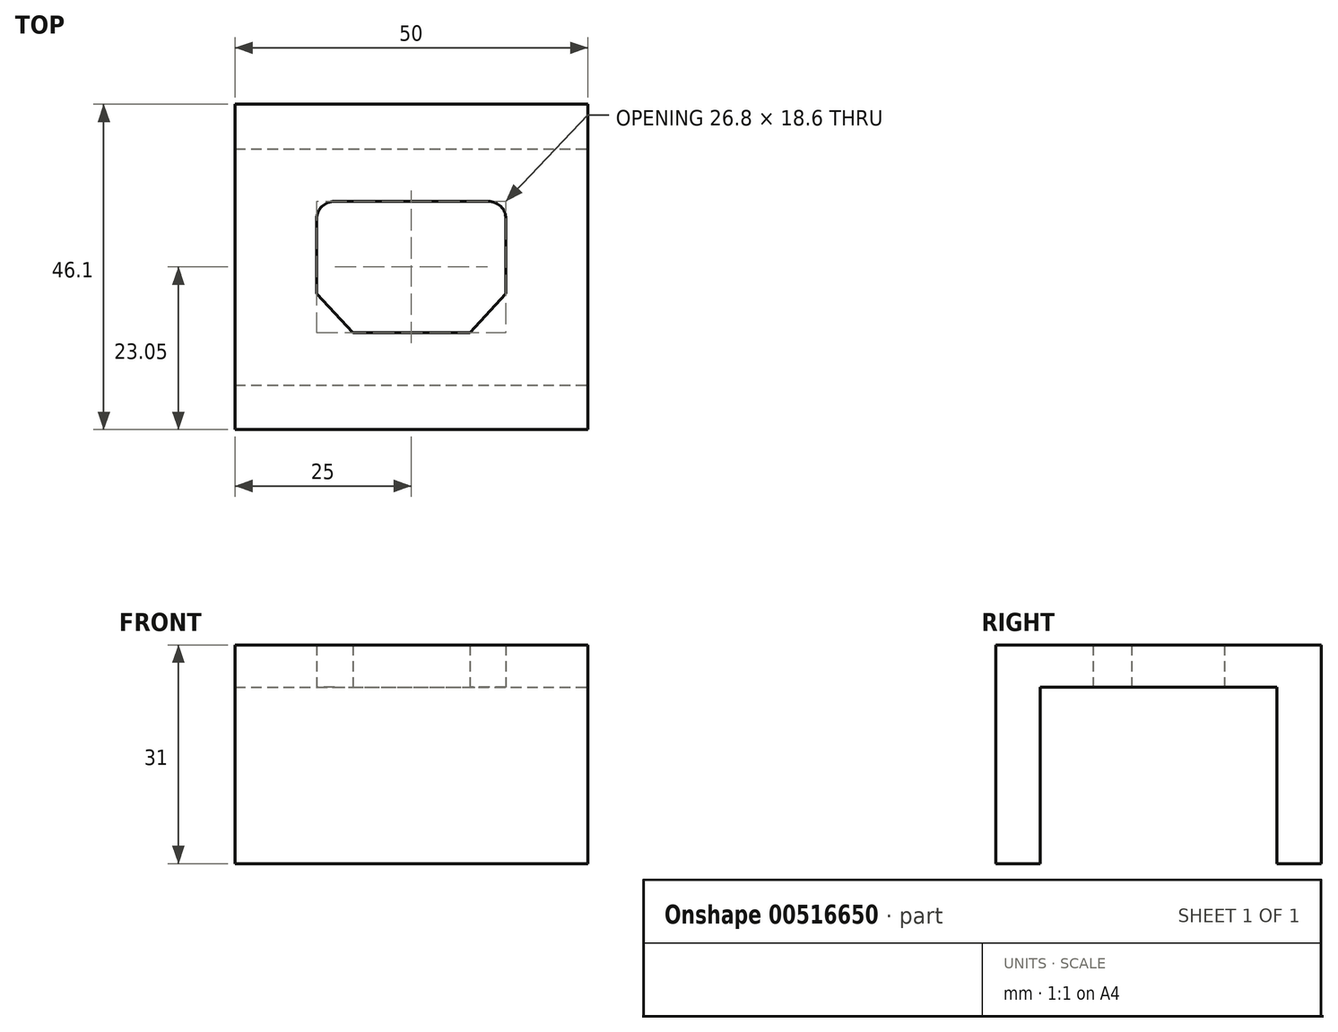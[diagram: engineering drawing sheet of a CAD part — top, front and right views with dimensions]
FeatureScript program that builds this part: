
annotation { "Feature Type Name" : "Feature", "Feature Type Description" : "" }
export const myFeature = defineFeature(function(context is Context, id is Id, definition is map)
    precondition{}
    {
        {
            var Q0;
            Q0=qCreatedBy(makeId("Top.planeOp"),FACE);
            var sketch = newSketch(context, id + "F0", { "sketchPlane" : qUnion([Q0])});
            skLineSegment(sketch, "E0.bottom", {"start": v(-25, 23.05) * mm, "end": v(25, 23.05) * mm});
            skLineSegment(sketch, "E0.top", {"start": v(-25, -23.05) * mm, "end": v(25, -23.05) * mm});
            skLineSegment(sketch, "E0.left", {"start": v(-25, 23.05) * mm, "end": v(-25, -23.05) * mm});
            skLineSegment(sketch, "E0.right", {"start": v(25, 23.05) * mm, "end": v(25, -23.05) * mm});
            skLineSegment(sketch, "E1.bottom", {"start": v(-10.9, 9.3) * mm, "end": v(10.9, 9.3) * mm});
            skLineSegment(sketch, "E1.top", {"start": v(-8.3, -9.3) * mm, "end": v(8.3, -9.3) * mm});
            skLineSegment(sketch, "E1.left", {"start": v(-13.4, 6.8) * mm, "end": v(-13.4, -3.8) * mm});
            skLineSegment(sketch, "E1.right", {"start": v(13.4, 6.8) * mm, "end": v(13.4, -3.8) * mm});
            skLineSegment(sketch, "E2", {"start": v(13.4, -3.8) * mm, "end": v(8.3, -9.3) * mm});
            skLineSegment(sketch, "E3.MirrorCS", {"start": v(-13.4, -3.8) * mm, "end": v(-8.3, -9.3) * mm});
            skPoint(sketch, "E4.orphan", {"position": v(13.4, -9.3) * mm});
            skPoint(sketch, "E5.visualSharp", {"position": v(-13.4, 9.3) * mm});
            skArc(sketch, "E5.filletArc", {"start": v(-10.9, 9.3) * mm, "mid": v(-12.67, 8.57) * mm, "end": v(-13.4, 6.8) * mm});
            skPoint(sketch, "E6.visualSharp", {"position": v(13.4, 9.3) * mm});
            skArc(sketch, "E6.filletArc", {"start": v(13.4, 6.8) * mm, "mid": v(12.67, 8.57) * mm, "end": v(10.9, 9.3) * mm});
            skCircle(sketch, "E7", {"center": v(-19.95, 0) * mm, "radius": 1.75 * mm});
            skCircle(sketch, "E8", {"center": v(19.95, 0) * mm, "radius": 1.75 * mm});
            skSolve(sketch);
        }
        {
            var Q0;
            Q0=makeQuery(id+"F0.imprint","IMPRINT",FACE,{"disambiguationData":[TD([[makeQuery(id+"F0.imprint","IMPRINT",EDGE,{"derivedFrom":sQuery(id+"F0.wireOp",EDGE,"E0.bottom")}),-1.0]])]});
            var Q1;
            Q1=makeQuery(id+"F0.imprint","IMPRINT",FACE,{"disambiguationData":[TD([[makeQuery(id+"F0.imprint","IMPRINT",EDGE,{"derivedFrom":sQuery(id+"F0.wireOp",EDGE,"E7")}),1.0]])]});
            var Q2;
            Q2=makeQuery(id+"F0.imprint","IMPRINT",FACE,{"disambiguationData":[TD([[makeQuery(id+"F0.imprint","IMPRINT",EDGE,{"derivedFrom":sQuery(id+"F0.wireOp",EDGE,"E8")}),1.0]])]});
            extrude(context, id + "F1", {"entities" : qUnion([Q0, Q1, Q2]), "depth" : 6 * mm, "offsetDistance" : 25 * mm});
        }
        {
            var Q0;
            Q0=makeQuery(id+"F0.imprint","IMPRINT",FACE,{"disambiguationData":[TD([[makeQuery(id+"F0.imprint","IMPRINT",EDGE,{"derivedFrom":sQuery(id+"F0.wireOp",EDGE,"E0.bottom")}),-1.0]])]});
            var sketch = newSketch(context, id + "F2", { "sketchPlane" : qUnion([Q0])});
            skLineSegment(sketch, "E9.0.0", {"start": v(-25, 23.05) * mm, "end": v(-25, -23.05) * mm});
            skLineSegment(sketch, "E9.0.1", {"start": v(-25, -23.05) * mm, "end": v(25, -23.05) * mm});
            skLineSegment(sketch, "E9.0.2", {"start": v(25, -23.05) * mm, "end": v(25, 23.05) * mm});
            skLineSegment(sketch, "E9.0.3", {"start": v(25, 23.05) * mm, "end": v(-25, 23.05) * mm});
            skLineSegment(sketch, "E10", {"start": v(-25, 16.75) * mm, "end": v(25, 16.75) * mm});
            skLineSegment(sketch, "E11", {"start": v(-25, -16.75) * mm, "end": v(25, -16.75) * mm});
            skSolve(sketch);
        }
        {
            var Q0;
            {var subQ0=sQuery(id+"F2.wireOp",EDGE,"E9.0.3");Q0=makeQuery(id+"F2.imprint","IMPRINT",FACE,{"disambiguationData":[TD([[makeQuery(id+"F2.imprint","IMPRINT",EDGE,{"derivedFrom":subQ0}),-1.0]])]});}
            var Q1;
            {var subQ0=sQuery(id+"F2.wireOp",EDGE,"E9.0.1");Q1=makeQuery(id+"F2.imprint","IMPRINT",FACE,{"disambiguationData":[TD([[makeQuery(id+"F2.imprint","IMPRINT",EDGE,{"derivedFrom":subQ0}),1.0]])]});}
            extrude(context, id + "F3", {"entities" : qUnion([Q0, Q1]), "operationType" : NewBodyOperationType.ADD, "oppositeDirection" : true, "depth" : 25 * mm, "offsetDistance" : 25 * mm});
        }
    });
